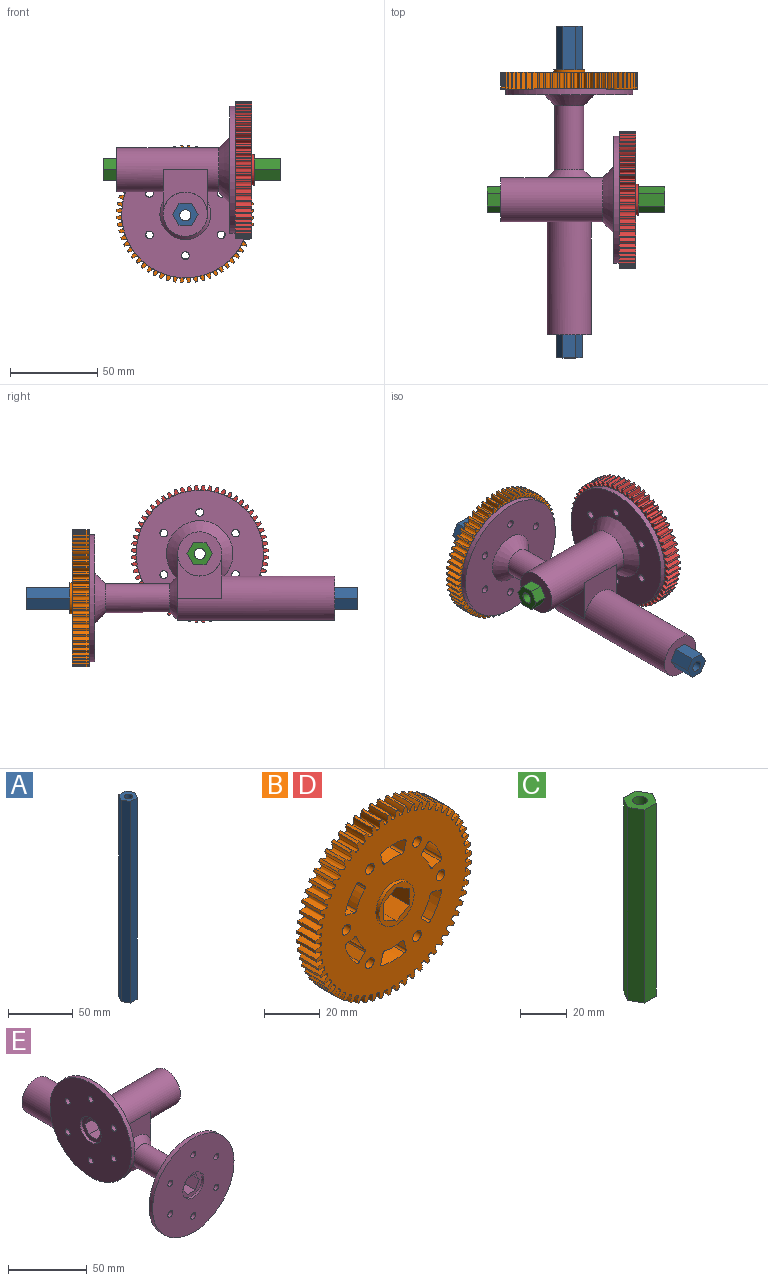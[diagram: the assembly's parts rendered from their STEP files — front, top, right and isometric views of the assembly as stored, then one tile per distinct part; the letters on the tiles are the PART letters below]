
ASSEMBLY  parts=5 mates=4
PART A: 9 faces, bbox 14.7x12.7x190.5 mm
  f0: plane 190.5x7.33mm, normal (0,1,0), area 1396.8mm2, adj f1,f5,f7,f8
  f1: plane 190.5x6.35mm, normal (-0.87,0.5,0), area 1396.8mm2, adj f0,f2,f7,f8
  f2: plane 190.5x6.35mm, normal (-0.87,-0.5,0), area 1396.8mm2, adj f1,f3,f7,f8
  f3: plane 190.5x7.33mm, normal (0,-1,0), area 1396.8mm2, adj f2,f4,f7,f8
  f4: plane 190.5x6.35mm, normal (0.87,-0.5,0), area 1396.8mm2, adj f3,f5,f7,f8
  f5: plane 190.5x6.35mm, normal (0.87,0.5,0), area 1396.8mm2, adj f0,f4,f7,f8
  f6: cylinder r=3.17mm len=190.5mm, axis (0,0,-1), area 3800.3mm2, adj f7,f8
  f7: plane 14.66x12.7mm, normal (0,0,1), area 108mm2, adj f0,f1,f2,f3,f4,f5,f6
  f8: plane 14.66x12.7mm, normal (0,0,-1), area 108mm2, adj f0,f1,f2,f3,f4,f5,f6
PART B: 186 faces, bbox 78.7x12.6x78.7 mm
  f0: cylinder r=2.15mm len=9.53mm, axis (0,1,0), area 128.7mm2, adj f14,f15
  f1: cylinder r=1mm len=9.53mm, axis (0,1,0), area 14.5mm2, adj f14,f15,f179,f185
  f2: cylinder r=2.15mm len=9.53mm, axis (0,1,0), area 128.7mm2, adj f14,f15
  f3: cylinder r=1mm len=9.53mm, axis (0,1,0), area 15.3mm2, adj f14,f15,f177,f178
  f4: cylinder r=2.15mm len=9.53mm, axis (0,1,0), area 128.7mm2, adj f14,f15
  f5: cylinder r=1mm len=9.53mm, axis (0,1,0), area 15.3mm2, adj f14,f15,f170,f171
  f6: cylinder r=2.15mm len=9.53mm, axis (0,1,0), area 128.7mm2, adj f14,f15
  f7: cylinder r=1mm len=9.53mm, axis (0,1,0), area 15.3mm2, adj f14,f15,f161,f162
  f8: cylinder r=2.15mm len=9.53mm, axis (0,1,0), area 128.7mm2, adj f14,f15
  f9: cylinder r=1mm len=9.53mm, axis (0,1,0), area 15.3mm2, adj f14,f15,f154,f155
  f10: cylinder r=2.15mm len=9.53mm, axis (0,1,0), area 128.7mm2, adj f14,f15
  f11: cylinder r=1mm len=9.53mm, axis (0,1,0), area 14.5mm2, adj f14,f15,f145,f146
  f12: cylinder r=8.89mm len=17.78mm, axis (0,1,0), area 87.3mm2, adj f14,f137
  f13: cylinder r=8.89mm len=17.78mm, axis (0,1,0), area 87.3mm2, adj f15,f136
  f14: plane 78.68x78.68mm, normal (0,-1,0), area 3765.5mm2, adj f0,f1,f2,f3,f4,f5,f6,f7
  f15: plane 78.68x78.68mm, normal (0,1,0), area 3765.5mm2, adj f0,f1,f2,f3,f4,f5,f6,f7
  f16: cylinder r=39.37mm len=9.53mm, axis (0,-1,0), area 11mm2, adj f14,f15,f134,f135
  f17: cylinder r=39.37mm len=9.53mm, axis (0,-1,0), area 11mm2, adj f14,f15,f76,f135
  f18: cylinder r=39.37mm len=9.53mm, axis (0,-1,0), area 11mm2, adj f14,f15,f133,f134
  f19: cylinder r=39.37mm len=9.53mm, axis (0,-1,0), area 11mm2, adj f14,f15,f132,f133
  f20: cylinder r=39.37mm len=9.53mm, axis (0,-1,0), area 11mm2, adj f14,f15,f131,f132
  f21: cylinder r=39.37mm len=9.53mm, axis (0,-1,0), area 11mm2, adj f14,f15,f130,f131
  f22: cylinder r=39.37mm len=9.53mm, axis (0,-1,0), area 11mm2, adj f14,f15,f129,f130
  f23: cylinder r=39.37mm len=9.53mm, axis (0,-1,0), area 11mm2, adj f14,f15,f128,f129
  f24: cylinder r=39.37mm len=9.53mm, axis (0,-1,0), area 11mm2, adj f14,f15,f127,f128
  f25: cylinder r=39.37mm len=9.53mm, axis (0,-1,0), area 11mm2, adj f14,f15,f126,f127
  f26: cylinder r=39.37mm len=9.53mm, axis (0,-1,0), area 11mm2, adj f14,f15,f125,f126
  f27: cylinder r=39.37mm len=9.53mm, axis (0,-1,0), area 11mm2, adj f14,f15,f124,f125
  f28: cylinder r=39.37mm len=9.53mm, axis (0,-1,0), area 11mm2, adj f14,f15,f123,f124
  f29: cylinder r=39.37mm len=9.53mm, axis (0,-1,0), area 11mm2, adj f14,f15,f122,f123
  f30: cylinder r=39.37mm len=9.53mm, axis (0,-1,0), area 11mm2, adj f14,f15,f121,f122
  f31: cylinder r=39.37mm len=9.53mm, axis (0,-1,0), area 11mm2, adj f14,f15,f120,f121
  f32: cylinder r=39.37mm len=9.53mm, axis (0,-1,0), area 11mm2, adj f14,f15,f119,f120
  f33: cylinder r=39.37mm len=9.53mm, axis (0,-1,0), area 11mm2, adj f14,f15,f118,f119
  f34: cylinder r=39.37mm len=9.53mm, axis (0,-1,0), area 11mm2, adj f14,f15,f117,f118
  f35: cylinder r=39.37mm len=9.53mm, axis (0,-1,0), area 11mm2, adj f14,f15,f116,f117
  f36: cylinder r=39.37mm len=9.53mm, axis (0,-1,0), area 11mm2, adj f14,f15,f115,f116
  f37: cylinder r=39.37mm len=9.53mm, axis (0,-1,0), area 11mm2, adj f14,f15,f114,f115
  f38: cylinder r=39.37mm len=9.53mm, axis (0,-1,0), area 11mm2, adj f14,f15,f113,f114
  f39: cylinder r=39.37mm len=9.53mm, axis (0,-1,0), area 11mm2, adj f14,f15,f112,f113
  f40: cylinder r=39.37mm len=9.53mm, axis (0,-1,0), area 11mm2, adj f14,f15,f111,f112
  f41: cylinder r=39.37mm len=9.53mm, axis (0,-1,0), area 11mm2, adj f14,f15,f110,f111
  f42: cylinder r=39.37mm len=9.53mm, axis (0,-1,0), area 11mm2, adj f14,f15,f109,f110
  f43: cylinder r=39.37mm len=9.53mm, axis (0,-1,0), area 11mm2, adj f14,f15,f108,f109
  f44: cylinder r=39.37mm len=9.53mm, axis (0,-1,0), area 11mm2, adj f14,f15,f107,f108
  f45: cylinder r=39.37mm len=9.53mm, axis (0,-1,0), area 11mm2, adj f14,f15,f106,f107
  f46: cylinder r=39.37mm len=9.53mm, axis (0,-1,0), area 11mm2, adj f14,f15,f105,f106
  f47: cylinder r=39.37mm len=9.53mm, axis (0,-1,0), area 11mm2, adj f14,f15,f104,f105
  f48: cylinder r=39.37mm len=9.53mm, axis (0,-1,0), area 11mm2, adj f14,f15,f103,f104
  f49: cylinder r=39.37mm len=9.53mm, axis (0,-1,0), area 11mm2, adj f14,f15,f102,f103
  f50: cylinder r=39.37mm len=9.53mm, axis (0,-1,0), area 11mm2, adj f14,f15,f101,f102
  f51: cylinder r=39.37mm len=9.53mm, axis (0,-1,0), area 11mm2, adj f14,f15,f100,f101
  f52: cylinder r=39.37mm len=9.53mm, axis (0,-1,0), area 11mm2, adj f14,f15,f99,f100
  f53: cylinder r=39.37mm len=9.53mm, axis (0,-1,0), area 11mm2, adj f14,f15,f98,f99
  f54: cylinder r=39.37mm len=9.53mm, axis (0,-1,0), area 11mm2, adj f14,f15,f97,f98
  f55: cylinder r=39.37mm len=9.53mm, axis (0,-1,0), area 11mm2, adj f14,f15,f96,f97
  f56: cylinder r=39.37mm len=9.53mm, axis (0,-1,0), area 11mm2, adj f14,f15,f95,f96
  f57: cylinder r=39.37mm len=9.53mm, axis (0,-1,0), area 11mm2, adj f14,f15,f94,f95
  f58: cylinder r=39.37mm len=9.53mm, axis (0,-1,0), area 11mm2, adj f14,f15,f93,f94
  f59: cylinder r=39.37mm len=9.53mm, axis (0,-1,0), area 11mm2, adj f14,f15,f92,f93
  f60: cylinder r=39.37mm len=9.53mm, axis (0,-1,0), area 11mm2, adj f14,f15,f91,f92
  f61: cylinder r=39.37mm len=9.53mm, axis (0,-1,0), area 11mm2, adj f14,f15,f90,f91
  f62: cylinder r=39.37mm len=9.53mm, axis (0,-1,0), area 11mm2, adj f14,f15,f89,f90
  f63: cylinder r=39.37mm len=9.53mm, axis (0,-1,0), area 11mm2, adj f14,f15,f88,f89
  f64: cylinder r=39.37mm len=9.53mm, axis (0,-1,0), area 11mm2, adj f14,f15,f87,f88
  f65: cylinder r=39.37mm len=9.53mm, axis (0,-1,0), area 11mm2, adj f14,f15,f86,f87
  f66: cylinder r=39.37mm len=9.53mm, axis (0,-1,0), area 11mm2, adj f14,f15,f85,f86
  f67: cylinder r=39.37mm len=9.53mm, axis (0,-1,0), area 11mm2, adj f14,f15,f84,f85
  f68: cylinder r=39.37mm len=9.53mm, axis (0,-1,0), area 11mm2, adj f14,f15,f83,f84
  f69: cylinder r=39.37mm len=9.53mm, axis (0,-1,0), area 11mm2, adj f14,f15,f82,f83
  f70: cylinder r=39.37mm len=9.53mm, axis (0,-1,0), area 11mm2, adj f14,f15,f81,f82
  f71: cylinder r=39.37mm len=9.53mm, axis (0,-1,0), area 11mm2, adj f14,f15,f80,f81
  f72: cylinder r=39.37mm len=9.53mm, axis (0,-1,0), area 11mm2, adj f14,f15,f79,f80
  f73: cylinder r=39.37mm len=9.53mm, axis (0,-1,0), area 11mm2, adj f14,f15,f78,f79
  f74: cylinder r=39.37mm len=9.53mm, axis (0,-1,0), area 11mm2, adj f14,f15,f77,f78
  f75: cylinder r=39.37mm len=9.53mm, axis (0,-1,0), area 11mm2, adj f14,f15,f76,f77
  f76: bspline ~9.53x2.96mm, area 66.7mm2, adj f14,f15,f17,f75
  f77: bspline ~9.53x3mm, area 66.7mm2, adj f14,f15,f74,f75
  f78: bspline ~9.53x3.14mm, area 66.7mm2, adj f14,f15,f73,f74
  f79: bspline ~9.53x3.26mm, area 66.7mm2, adj f14,f15,f72,f73
  f80: bspline ~9.53x3.35mm, area 66.7mm2, adj f14,f15,f71,f72
  f81: bspline ~9.53x3.4mm, area 66.7mm2, adj f14,f15,f70,f71
  f82: bspline ~9.53x3.42mm, area 66.7mm2, adj f14,f15,f69,f70
  f83: bspline ~9.53x3.41mm, area 66.7mm2, adj f14,f15,f68,f69
  f84: bspline ~9.53x3.41mm, area 66.7mm2, adj f14,f15,f67,f68
  f85: bspline ~9.53x3.42mm, area 66.7mm2, adj f14,f15,f66,f67
  f86: bspline ~9.53x3.4mm, area 66.7mm2, adj f14,f15,f65,f66
  f87: bspline ~9.53x3.35mm, area 66.7mm2, adj f14,f15,f64,f65
  f88: bspline ~9.53x3.26mm, area 66.7mm2, adj f14,f15,f63,f64
  f89: bspline ~9.53x3.14mm, area 66.7mm2, adj f14,f15,f62,f63
  f90: bspline ~9.53x3mm, area 66.7mm2, adj f14,f15,f61,f62
  f91: bspline ~9.53x2.96mm, area 66.7mm2, adj f14,f15,f60,f61
  f92: bspline ~9.53x3mm, area 66.7mm2, adj f14,f15,f59,f60
  f93: bspline ~9.53x3.14mm, area 66.7mm2, adj f14,f15,f58,f59
  f94: bspline ~9.53x3.26mm, area 66.7mm2, adj f14,f15,f57,f58
  f95: bspline ~9.53x3.35mm, area 66.7mm2, adj f14,f15,f56,f57
  f96: bspline ~9.53x3.4mm, area 66.7mm2, adj f14,f15,f55,f56
  f97: bspline ~9.53x3.42mm, area 66.7mm2, adj f14,f15,f54,f55
  f98: bspline ~9.53x3.41mm, area 66.7mm2, adj f14,f15,f53,f54
  f99: bspline ~9.53x3.41mm, area 66.7mm2, adj f14,f15,f52,f53
  f100: bspline ~9.53x3.42mm, area 66.7mm2, adj f14,f15,f51,f52
  f101: bspline ~9.53x3.4mm, area 66.7mm2, adj f14,f15,f50,f51
  f102: bspline ~9.53x3.35mm, area 66.7mm2, adj f14,f15,f49,f50
  f103: bspline ~9.53x3.26mm, area 66.7mm2, adj f14,f15,f48,f49
  f104: bspline ~9.53x3.14mm, area 66.7mm2, adj f14,f15,f47,f48
  f105: bspline ~9.53x3mm, area 66.7mm2, adj f14,f15,f46,f47
  f106: bspline ~9.53x2.96mm, area 66.7mm2, adj f14,f15,f45,f46
  f107: bspline ~9.53x3mm, area 66.7mm2, adj f14,f15,f44,f45
  f108: bspline ~9.53x3.14mm, area 66.7mm2, adj f14,f15,f43,f44
  f109: bspline ~9.53x3.26mm, area 66.7mm2, adj f14,f15,f42,f43
  f110: bspline ~9.53x3.35mm, area 66.7mm2, adj f14,f15,f41,f42
  f111: bspline ~9.53x3.4mm, area 66.7mm2, adj f14,f15,f40,f41
  f112: bspline ~9.53x3.42mm, area 66.7mm2, adj f14,f15,f39,f40
  f113: bspline ~9.53x3.41mm, area 66.7mm2, adj f14,f15,f38,f39
  f114: bspline ~9.53x3.41mm, area 66.7mm2, adj f14,f15,f37,f38
  f115: bspline ~9.53x3.42mm, area 66.7mm2, adj f14,f15,f36,f37
  f116: bspline ~9.53x3.4mm, area 66.7mm2, adj f14,f15,f35,f36
  f117: bspline ~9.53x3.35mm, area 66.7mm2, adj f14,f15,f34,f35
  f118: bspline ~9.53x3.26mm, area 66.7mm2, adj f14,f15,f33,f34
  f119: bspline ~9.53x3.14mm, area 66.7mm2, adj f14,f15,f32,f33
  f120: bspline ~9.53x3mm, area 66.7mm2, adj f14,f15,f31,f32
  f121: bspline ~9.53x2.96mm, area 66.7mm2, adj f14,f15,f30,f31
  f122: bspline ~9.53x3mm, area 66.7mm2, adj f14,f15,f29,f30
  f123: bspline ~9.53x3.14mm, area 66.7mm2, adj f14,f15,f28,f29
  f124: bspline ~9.53x3.26mm, area 66.7mm2, adj f14,f15,f27,f28
  f125: bspline ~9.53x3.35mm, area 66.7mm2, adj f14,f15,f26,f27
  f126: bspline ~9.53x3.4mm, area 66.7mm2, adj f14,f15,f25,f26
  f127: bspline ~9.53x3.42mm, area 66.7mm2, adj f14,f15,f24,f25
  f128: bspline ~9.53x3.41mm, area 66.7mm2, adj f14,f15,f23,f24
  f129: bspline ~9.53x3.41mm, area 66.7mm2, adj f14,f15,f22,f23
  f130: bspline ~9.53x3.42mm, area 66.7mm2, adj f14,f15,f21,f22
  f131: bspline ~9.53x3.4mm, area 66.7mm2, adj f14,f15,f20,f21
  f132: bspline ~9.53x3.35mm, area 66.7mm2, adj f14,f15,f19,f20
  f133: bspline ~9.53x3.26mm, area 66.7mm2, adj f14,f15,f18,f19
  f134: bspline ~9.53x3.14mm, area 66.7mm2, adj f14,f15,f16,f18
  f135: bspline ~9.53x3mm, area 66.7mm2, adj f14,f15,f16,f17
  f136: plane 17.78x17.78mm, normal (0,1,0), area 106.9mm2, adj f13,f138,f139,f140,f141,f142,f143
  f137: plane 17.78x17.78mm, normal (0,-1,0), area 106.9mm2, adj f12,f138,f139,f140,f141,f142,f143
  f138: plane 12.65x7.38mm, normal (1,0,0), area 93.3mm2, adj f136,f137,f139,f143
  f139: plane 12.65x6.39mm, normal (0.5,0,0.87), area 93.3mm2, adj f136,f137,f138,f140
  f140: plane 12.65x6.39mm, normal (-0.5,0,0.87), area 93.3mm2, adj f136,f137,f139,f141
  f141: plane 12.65x7.38mm, normal (-1,0,0), area 93.3mm2, adj f136,f137,f140,f142
  f142: plane 12.65x6.39mm, normal (-0.5,0,-0.87), area 93.3mm2, adj f136,f137,f141,f143
  f143: plane 12.65x6.39mm, normal (0.5,0,-0.87), area 93.3mm2, adj f136,f137,f138,f142
  f144: cylinder r=1mm len=9.53mm, axis (0,1,0), area 14.5mm2, adj f14,f15,f145,f150
  f145: cylinder r=19.5mm len=9.53mm, axis (0,1,0), area 79.8mm2, adj f11,f14,f15,f144
  f146: plane 9.53x2.83mm, normal (0.71,0,0.71), area 38.1mm2, adj f11,f14,f15,f147
  f147: cylinder r=1mm len=9.53mm, axis (0,1,0), area 15.3mm2, adj f14,f15,f146,f148
  f148: cylinder r=25.5mm len=9.75mm, axis (0,1,0), area 108.1mm2, adj f14,f15,f147,f149
  f149: cylinder r=1mm len=9.53mm, axis (0,1,0), area 15.3mm2, adj f14,f15,f148,f150
  f150: plane 9.53x3.87mm, normal (-0.26,0,-0.97), area 38.1mm2, adj f14,f15,f144,f149
  f151: cylinder r=1mm len=9.53mm, axis (0,1,0), area 14.5mm2, adj f14,f15,f152,f157
  f152: cylinder r=19.5mm len=9.53mm, axis (0,1,0), area 79.8mm2, adj f14,f15,f151,f153
  f153: cylinder r=1mm len=9.53mm, axis (0,1,0), area 14.5mm2, adj f14,f15,f152,f154
  f154: plane 9.53x3.87mm, normal (0.97,0,-0.26), area 38.1mm2, adj f9,f14,f15,f153
  f155: cylinder r=25.5mm len=11.26mm, axis (0,1,0), area 108.1mm2, adj f9,f14,f15,f156
  f156: cylinder r=1mm len=9.53mm, axis (0,1,0), area 15.3mm2, adj f14,f15,f155,f157
  f157: plane 9.53x3.87mm, normal (-0.97,0,-0.26), area 38.1mm2, adj f14,f15,f151,f156
  f158: cylinder r=1mm len=9.53mm, axis (0,1,0), area 14.5mm2, adj f14,f15,f159,f164
  f159: cylinder r=19.5mm len=9.53mm, axis (0,1,0), area 79.8mm2, adj f14,f15,f158,f160
  f160: cylinder r=1mm len=9.53mm, axis (0,1,0), area 14.5mm2, adj f14,f15,f159,f161
  f161: plane 9.53x3.87mm, normal (0.26,0,-0.97), area 38.1mm2, adj f7,f14,f15,f160
  f162: cylinder r=25.5mm len=9.74mm, axis (0,1,0), area 108.1mm2, adj f7,f14,f15,f163
  f163: cylinder r=1mm len=9.53mm, axis (0,1,0), area 15.3mm2, adj f14,f15,f162,f164
  f164: plane 9.53x2.83mm, normal (-0.71,0,0.71), area 38.1mm2, adj f14,f15,f158,f163
  f165: cylinder r=1mm len=9.53mm, axis (0,1,0), area 14.5mm2, adj f14,f15,f166,f171
  f166: cylinder r=19.5mm len=9.53mm, axis (0,1,0), area 79.8mm2, adj f14,f15,f165,f167
  f167: cylinder r=1mm len=9.53mm, axis (0,1,0), area 14.5mm2, adj f14,f15,f166,f168
  f168: plane 9.53x2.83mm, normal (-0.71,0,-0.71), area 38.1mm2, adj f14,f15,f167,f169
  f169: cylinder r=1mm len=9.53mm, axis (0,1,0), area 15.3mm2, adj f14,f15,f168,f170
  f170: cylinder r=25.5mm len=9.75mm, axis (0,1,0), area 108.1mm2, adj f5,f14,f15,f169
  f171: plane 9.53x3.87mm, normal (0.26,0,0.97), area 38.1mm2, adj f5,f14,f15,f165
  f172: cylinder r=1mm len=9.53mm, axis (0,1,0), area 14.5mm2, adj f14,f15,f173,f178
  f173: cylinder r=19.5mm len=9.53mm, axis (0,1,0), area 79.8mm2, adj f14,f15,f172,f174
  f174: cylinder r=1mm len=9.53mm, axis (0,1,0), area 14.5mm2, adj f14,f15,f173,f175
  f175: plane 9.53x3.87mm, normal (-0.97,0,0.26), area 38.1mm2, adj f14,f15,f174,f176
  f176: cylinder r=1mm len=9.53mm, axis (0,1,0), area 15.3mm2, adj f14,f15,f175,f177
  f177: cylinder r=25.5mm len=11.26mm, axis (0,1,0), area 108.1mm2, adj f3,f14,f15,f176
  f178: plane 9.53x3.87mm, normal (0.97,0,0.26), area 38.1mm2, adj f3,f14,f15,f172
  f179: cylinder r=19.5mm len=9.53mm, axis (0,1,0), area 79.8mm2, adj f1,f14,f15,f180
  f180: cylinder r=1mm len=9.53mm, axis (0,1,0), area 14.5mm2, adj f14,f15,f179,f181
  f181: plane 9.53x3.87mm, normal (-0.26,0,0.97), area 38.1mm2, adj f14,f15,f180,f182
  f182: cylinder r=1mm len=9.53mm, axis (0,1,0), area 15.3mm2, adj f14,f15,f181,f183
  f183: cylinder r=25.5mm len=9.74mm, axis (0,1,0), area 108.1mm2, adj f14,f15,f182,f184
  f184: cylinder r=1mm len=9.53mm, axis (0,1,0), area 15.3mm2, adj f14,f15,f183,f185
  f185: plane 9.53x2.83mm, normal (0.71,0,-0.71), area 38.1mm2, adj f1,f14,f15,f184
PART C: 9 faces, bbox 14.7x12.7x101.6 mm
  f0: plane 101.6x7.33mm, normal (0,1,0), area 745mm2, adj f1,f5,f7,f8
  f1: plane 101.6x6.35mm, normal (-0.87,0.5,0), area 745mm2, adj f0,f2,f7,f8
  f2: plane 101.6x6.35mm, normal (-0.87,-0.5,0), area 745mm2, adj f1,f3,f7,f8
  f3: plane 101.6x7.33mm, normal (0,-1,0), area 745mm2, adj f2,f4,f7,f8
  f4: plane 101.6x6.35mm, normal (0.87,-0.5,0), area 745mm2, adj f3,f5,f7,f8
  f5: plane 101.6x6.35mm, normal (0.87,0.5,0), area 745mm2, adj f0,f4,f7,f8
  f6: cylinder r=3.17mm len=101.6mm, axis (0,0,-1), area 2026.8mm2, adj f7,f8
  f7: plane 14.66x12.7mm, normal (0,0,1), area 108mm2, adj f0,f1,f2,f3,f4,f5,f6
  f8: plane 14.66x12.7mm, normal (0,0,-1), area 108mm2, adj f0,f1,f2,f3,f4,f5,f6
PART D: same geometry as B
PART E: 46 faces, bbox 75.9x141x98.4 mm
  f0: plane 25.4x25.4mm, normal (0,1,0), area 391.8mm2, adj f13,f15,f16,f18
  f1: plane 66.04x7.33mm, normal (0,0,-1), area 484.2mm2, adj f2,f6,f42,f44
  f2: plane 66.04x6.35mm, normal (0,-0.87,-0.5), area 484.2mm2, adj f1,f3,f42,f44
  f3: plane 66.04x6.35mm, normal (0,-0.87,0.5), area 484.2mm2, adj f2,f4,f42,f44
  f4: plane 66.04x7.33mm, normal (0,0,1), area 484.2mm2, adj f3,f5,f42,f44
  f5: plane 66.04x6.35mm, normal (0,0.87,0.5), area 484.2mm2, adj f4,f6,f42,f44
  f6: plane 66.04x6.35mm, normal (0,0.87,-0.5), area 484.2mm2, adj f1,f5,f42,f44
  f7: plane 139.07x7.33mm, normal (0,0,-1), area 1019.7mm2, adj f8,f12,f40,f45
  f8: plane 139.07x6.35mm, normal (0.87,0,-0.5), area 1019.7mm2, adj f7,f9,f40,f45
  f9: plane 139.07x6.35mm, normal (0.87,0,0.5), area 1019.7mm2, adj f8,f10,f40,f45
  f10: plane 139.07x7.33mm, normal (0,0,1), area 1019.7mm2, adj f9,f11,f40,f45
  f11: plane 139.07x6.35mm, normal (-0.87,0,0.5), area 1019.7mm2, adj f10,f12,f40,f45
  f12: plane 139.07x6.35mm, normal (-0.87,0,-0.5), area 1019.7mm2, adj f7,f11,f40,f45
  f13: cylinder r=12.7mm len=58.42mm, axis (-1,0,0), area 3648.3mm2, adj f0,f15,f16,f17,f43,f44
  f14: cylinder r=8.26mm len=36.83mm, axis (0,1,0), area 1910.3mm2, adj f20,f29
  f15: plane 25.4x25.4mm, normal (-1,0,0), area 391.8mm2, adj f0,f13,f17,f18
  f16: plane 25.4x25.4mm, normal (1,0,0), area 391.8mm2, adj f0,f13,f17,f18
  f17: plane 25.4x25.4mm, normal (0,-1,0), area 391.8mm2, adj f13,f15,f16,f20
  f18: cylinder r=12.7mm len=90.17mm, axis (0,-1,0), area 6181.8mm2, adj f0,f15,f16,f20,f45
  f19: plane 73.03x73.03mm, normal (0,-1,0), area 3810.1mm2, adj f21,f23,f24,f25,f26,f27,f28,f39
  f20: cone r=8.26mm half-angle=45deg, axis (0,1,0), area 413.8mm2, adj f14,f17,f18
  f21: cylinder r=36.51mm len=73.03mm, axis (0,-1,0), area 728.4mm2, adj f19,f22
  f22: plane 73.03x73.03mm, normal (0,1,0), area 3425mm2, adj f21,f23,f24,f25,f26,f27,f28,f29
  f23: cylinder r=2.22mm len=4.45mm, axis (0,-1,0), area 44.3mm2, adj f19,f22
  f24: cylinder r=2.22mm len=4.45mm, axis (0,-1,0), area 44.3mm2, adj f19,f22
  f25: cylinder r=2.22mm len=4.45mm, axis (0,-1,0), area 44.3mm2, adj f19,f22
  f26: cylinder r=2.22mm len=4.45mm, axis (0,-1,0), area 44.3mm2, adj f19,f22
  f27: cylinder r=2.22mm len=4.45mm, axis (0,-1,0), area 44.3mm2, adj f19,f22
  f28: cylinder r=2.22mm len=4.45mm, axis (0,-1,0), area 44.3mm2, adj f19,f22
  f29: cone r=14.61mm half-angle=45deg, axis (0,-1,0), area 644.9mm2, adj f14,f22
  f30: plane 73.03x73.03mm, normal (-1,0,0), area 3810.1mm2, adj f31,f33,f34,f35,f36,f37,f38,f41
  f31: cylinder r=36.51mm len=73.03mm, axis (-1,0,0), area 728.4mm2, adj f30,f32
  f32: plane 73.03x73.03mm, normal (1,0,0), area 2955.1mm2, adj f31,f33,f34,f35,f36,f37,f38,f43
  f33: cylinder r=2.22mm len=4.45mm, axis (-1,0,0), area 44.3mm2, adj f30,f32
  f34: cylinder r=2.22mm len=4.45mm, axis (-1,0,0), area 44.3mm2, adj f30,f32
  f35: cylinder r=2.22mm len=4.45mm, axis (-1,0,0), area 44.3mm2, adj f30,f32
  f36: cylinder r=2.22mm len=4.45mm, axis (-1,0,0), area 44.3mm2, adj f30,f32
  f37: cylinder r=2.22mm len=4.45mm, axis (-1,0,0), area 44.3mm2, adj f30,f32
  f38: cylinder r=2.22mm len=4.45mm, axis (-1,0,0), area 44.3mm2, adj f30,f32
  f39: cylinder r=9.53mm len=19.05mm, axis (0,-1,0), area 114mm2, adj f19,f40
  f40: plane 19.05x19.05mm, normal (0,-1,0), area 145.3mm2, adj f7,f8,f9,f10,f11,f12,f39
  f41: cylinder r=9.53mm len=19.05mm, axis (-1,0,0), area 114mm2, adj f30,f42
  f42: plane 19.05x19.05mm, normal (-1,0,0), area 145.3mm2, adj f1,f2,f3,f4,f5,f6,f41
  f43: cone r=12.7mm half-angle=45deg, axis (-1,0,0), area 895.7mm2, adj f13,f32
  f44: plane 25.4x25.4mm, normal (1,0,0), area 367mm2, adj f1,f2,f3,f4,f5,f6,f13
  f45: plane 25.4x25.4mm, normal (0,1,0), area 367mm2, adj f7,f8,f9,f10,f11,f12,f18
PLACE A rot(axis=(0,-0.71,-0.71),180deg) t=(0,-90.8,-0.66)mm
PLACE B rot(axis=(0,0,1),180deg) t=(0,68.26,0)mm
PLACE C rot(axis=(-0.58,0.58,-0.58),120deg) t=(-46.99,0,25.4)mm
PLACE D rot(axis=(0,0,1),90deg) t=(33.34,0,25.4)mm
PLACE E rot(axis=(0,0,1),180deg) t=(0,0,12.7)mm
MATE fastened A.f7 <-> E.f14  axis (0,1,0) through (0,99.7,0)mm
MATE fastened C.f6 <-> E.f41  axis (1,0,0) through (54.61,0,25.4)mm
MATE fastened B.f12 <-> E.f14  axis (0,-1,0) through (0,63.5,0)mm
MATE fastened D.f12 <-> E.f41  axis (-1,0,0) through (28.57,0,25.4)mm
